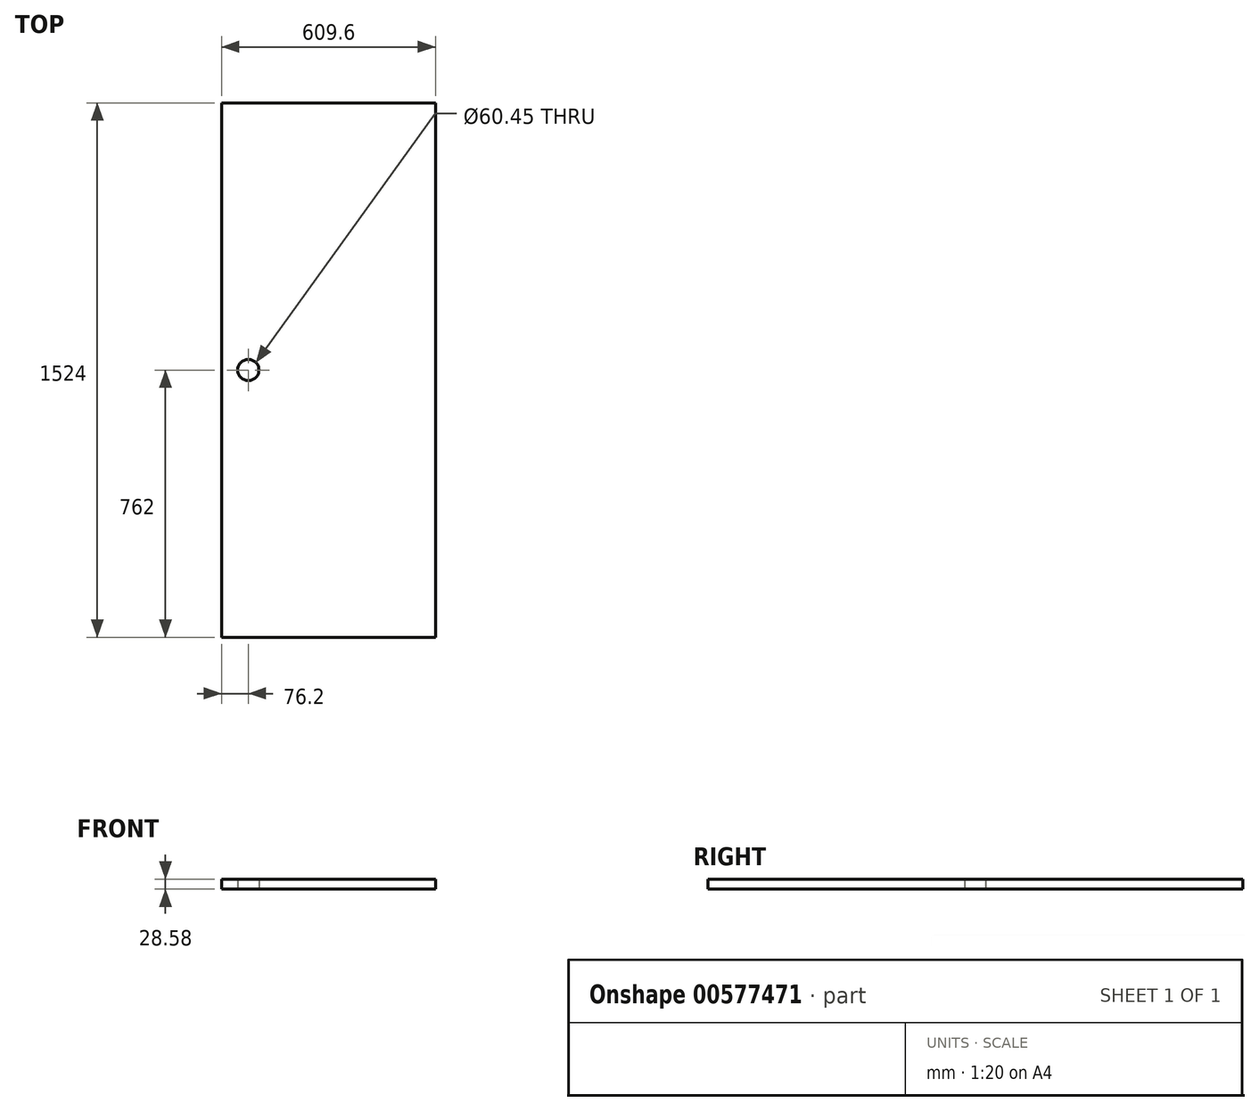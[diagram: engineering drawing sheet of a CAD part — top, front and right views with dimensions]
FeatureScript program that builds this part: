
annotation { "Feature Type Name" : "Feature", "Feature Type Description" : "" }
export const myFeature = defineFeature(function(context is Context, id is Id, definition is map)
    precondition{}
    {
        {
            var Q0;
            Q0=qCreatedBy(makeId("Top.planeOp"),FACE);
            var sketch = newSketch(context, id + "F0", { "sketchPlane" : qUnion([Q0])});
            skLineSegment(sketch, "E0.bottom", {"start": v(304.8, 762) * mm, "end": v(-304.8, 762) * mm});
            skLineSegment(sketch, "E0.top", {"start": v(304.8, -762) * mm, "end": v(-304.8, -762) * mm});
            skLineSegment(sketch, "E0.left", {"start": v(304.8, 762) * mm, "end": v(304.8, -762) * mm});
            skLineSegment(sketch, "E0.right", {"start": v(-304.8, 762) * mm, "end": v(-304.8, -762) * mm});
            skPoint(sketch, "E0.middle", {"position": v(0, 0) * mm});
            skLineSegment(sketch, "E1", {"start": v(-304.8, 0) * mm, "end": v(-228.6, 0) * mm});
            skPoint(sketch, "E1.endSnap0", {"position": v(-304.8, 0) * mm});
            skCircle(sketch, "E2", {"center": v(-228.6, 0) * mm, "radius": 30.23 * mm});
            skSolve(sketch);
        }
        {
            var Q0;
            Q0=makeQuery(id+"F0.imprint","IMPRINT",FACE,{"disambiguationData":[TD([[makeQuery(id+"F0.imprint","IMPRINT",EDGE,{"derivedFrom":sQuery(id+"F0.wireOp",EDGE,"E0.bottom")}),1.0]])]});
            extrude(context, id + "F1", {"entities" : qUnion([Q0]), "depth" : 28.57 * mm, "offsetDistance" : 25.4 * mm});
        }
    });
